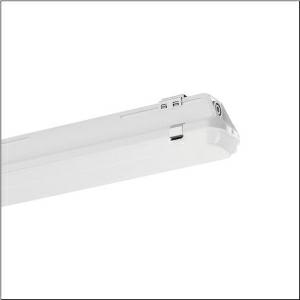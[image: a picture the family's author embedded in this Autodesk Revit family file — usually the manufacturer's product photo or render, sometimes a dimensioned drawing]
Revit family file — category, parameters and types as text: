
# Revit family: monsun_r__21_emergency_51fb107l447k3g_6241
name_source: partatom
category: Lighting Fixtures
units: mm (PartAtom-declared; Revit-internal decimal feet)

## family parameters
Cut with Voids When Loaded = No
Host = Face
Light Source = No
Part Type = Normal
Room Calculation Point = No
Round Connector Dimension = Use Diameter
Shared = No

## types (1)
- --- (1 x LED, 4330 lm, 28.8 W, 4000K)
    Apparent Load = 29 VA
    CIE Flux Codes = 46 76 93 94 100
    Color Rendering = 80
    Color Temperature = 4000K
    Default Elevation = 1800 mm
    Description = Monsun® 21 emergency, damp-proof luminaire, chain hanger, primary optical cover: enclosure, of PMMA, light emission: direct distribution, primary light characteristic: symmetric, installation type: suspended mounting, surface-mounted, horizontal mounting, vertical mounting, LED, rated luminous flux: 4.330lm, luminous efficacy: 173lm/W, light colour: 840, colour temperature: 4000K, control gear: ON/OFF, with terminal, 3-pole, max. 2.5mm², mains connection: 220..240V, AC, 50/60Hz, rated input power: 29W, control gear: single battery element, battery: LiFePO4, 9Ah, housing, of glass-fibre reinforced plastic, uncoated, bright grey, incl. chain hanger, length: 1.299mm, width: 90mm, height: 88mm, clip for enclosure, of stainless steel (V2A), ceiling mounting element, of stainless steel (V2A), chain hanger, of stainless steel (V2A), protection rating (complete): IP66, insulation class (complete): insulation class I (protective earthing), certification: CE, UKCA, protection symbol: D, impact resistance: IK04, permissible operating ambient temperature: +5..+25°C, standard: EN 50419, EN 60598-2-1, corresponds to IFS (International Featured Standards) requirements for safety and quality in the food industry, for indoor or canopied outdoor use, no direct snow, no direct sun, no direct rain, LABS conformity tested according to VDMA 24364:2018-05, contact your sales advisor before using the luminaires in applications with unclear chemical exposure, large temperature fluctuations or condensation-forming humidity, packaging unit: 1 piece
    Height = 88 mm
    Lamp = 1 x LED
    Lamp Light Flux = 4330 lm
    Lamp Power = 28.8 W
    Lamp count = 1
    Length = 1299 mm
    Luminous efficacy = 150 lm/W
    Manufacturer = Siteco
    ModVariant = No
    Model = 51FB107L447K3G
    Mounting Place = Ceiling
    Mounting Type = Surface mounted
    Number of Poles = 1
    OnlyDefault = Yes
    Power Factor = 1
    Product Name = Monsun® 21 emergency
    Product group = damp-proof luminaire
    ProductGroupID = 300
    Protection Class = Protection class I
    Protection Degree = IP 66
    RLX_Detail_Level = 1
    RLX_Emergency_Light_Flux = 0 lm
    RLX_Emergency_Type = 0
    RLX_Emergency_Type_DB = No
    RlxData = <blob elided: 90029 chars, md5=0aa427af>
    Socket = socket
    Standby Power = 0 W
    System Light Flux = 4330 lm
    System Power = 29 W
    Type Comments = -
    Type Image = l_1319656.jpg
    URL = http://relux.com
    VarID = @adj_021148
    Voltage = 0 V
    Weight = 0.00 kg
    Width = 90 mm

## geometry (parser evidence)
native form markers: Blend x4, Sweep x11
no freeform markers — native parametric forms only
